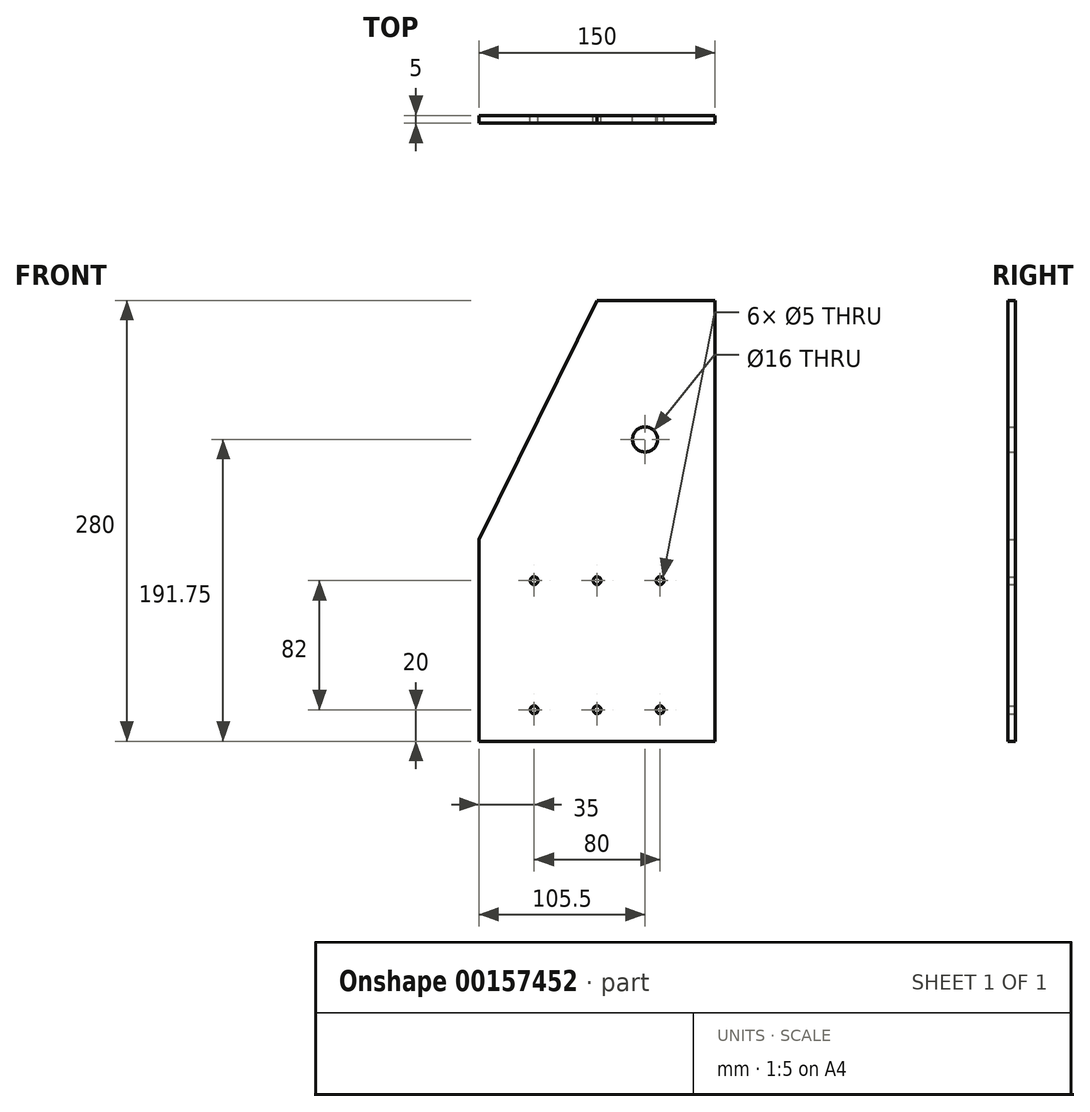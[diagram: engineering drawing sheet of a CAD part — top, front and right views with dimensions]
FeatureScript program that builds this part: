
annotation { "Feature Type Name" : "Feature", "Feature Type Description" : "" }
export const myFeature = defineFeature(function(context is Context, id is Id, definition is map)
    precondition{}
    {
        {
            var Q0;
            Q0=qCreatedBy(makeId("Front.planeOp"),FACE);
            var sketch = newSketch(context, id + "F0", { "sketchPlane" : qUnion([Q0])});
            skLineSegment(sketch, "E0.bottom", {"start": v(75, -140) * mm, "end": v(-75, -140) * mm});
            skLineSegment(sketch, "E0.top", {"start": v(75, 140) * mm, "end": v(0, 140) * mm});
            skLineSegment(sketch, "E0.left", {"start": v(75, -140) * mm, "end": v(75, 140) * mm});
            skLineSegment(sketch, "E0.right", {"start": v(-75, -140) * mm, "end": v(-75, -11.7) * mm});
            skPoint(sketch, "E0.middle", {"position": v(0, 0) * mm});
            skCircle(sketch, "E1", {"center": v(-40, -38) * mm, "radius": 2.5 * mm});
            skCircle(sketch, "E2", {"center": v(0, -38) * mm, "radius": 2.5 * mm});
            skCircle(sketch, "E3", {"center": v(-40, -120) * mm, "radius": 2.5 * mm});
            skCircle(sketch, "E4", {"center": v(0, -120) * mm, "radius": 2.5 * mm});
            skCircle(sketch, "E5", {"center": v(40, -120) * mm, "radius": 2.5 * mm});
            skCircle(sketch, "E6", {"center": v(40, -38) * mm, "radius": 2.5 * mm});
            skLineSegment(sketch, "E7", {"start": v(0, 140) * mm, "end": v(-75, -11.7) * mm});
            skPoint(sketch, "E8.orphan", {"position": v(-75, 140) * mm});
            skCircle(sketch, "E9", {"center": v(30.5, 51.75) * mm, "radius": 8 * mm});
            skSolve(sketch);
        }
        {
            var Q0;
            Q0=makeQuery(id+"F0.imprint","IMPRINT",FACE,{"disambiguationData":[TD([[makeQuery(id+"F0.imprint","IMPRINT",EDGE,{"derivedFrom":sQuery(id+"F0.wireOp",EDGE,"E0.bottom")}),-1.0]])]});
            extrude(context, id + "F1", {"entities" : qUnion([Q0]), "depth" : 5 * mm});
        }
    });
